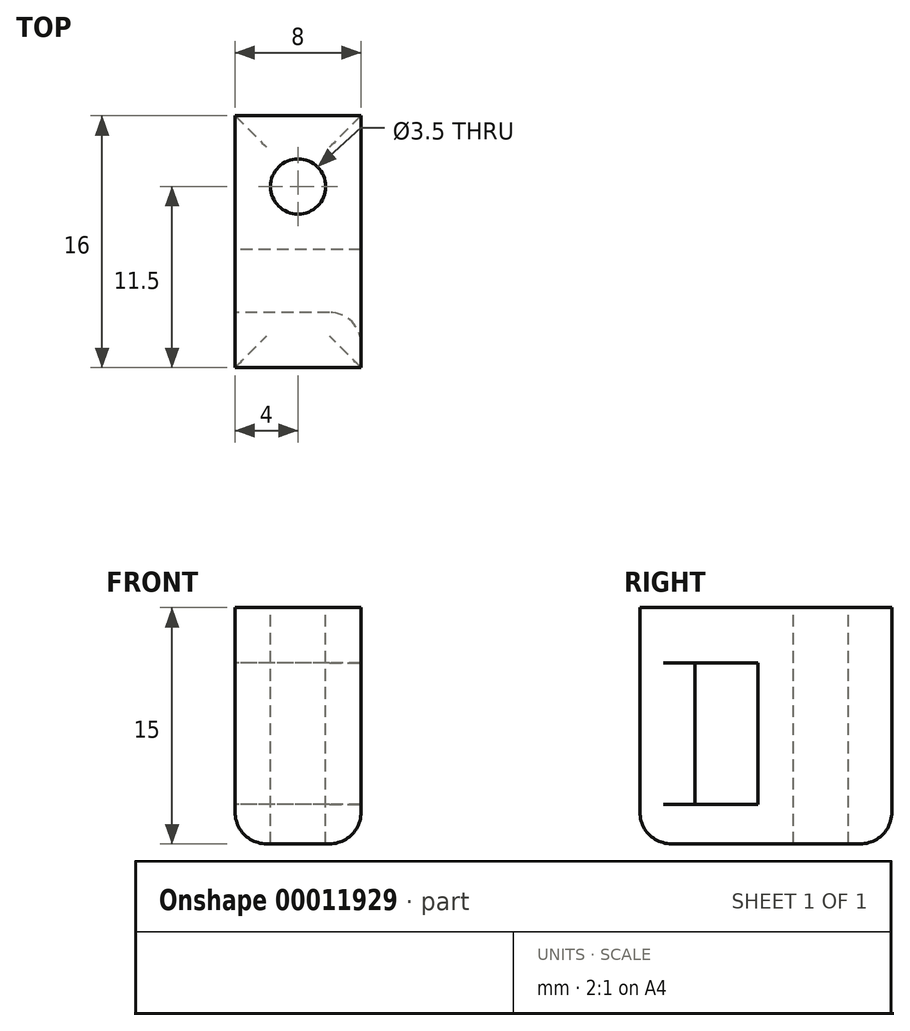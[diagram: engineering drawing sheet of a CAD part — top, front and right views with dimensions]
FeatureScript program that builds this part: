
annotation { "Feature Type Name" : "Feature", "Feature Type Description" : "" }
export const myFeature = defineFeature(function(context is Context, id is Id, definition is map)
    precondition{}
    {
        {
            var Q0;
            Q0=qCreatedBy(makeId("Top.planeOp"),FACE);
            var sketch = newSketch(context, id + "F0", { "sketchPlane" : qUnion([Q0])});
            skLineSegment(sketch, "E0.rect.bottom", {"start": v(-4, 8) * mm, "end": v(4, 8) * mm});
            skLineSegment(sketch, "E0.rect.top", {"start": v(-4, -8) * mm, "end": v(4, -8) * mm});
            skLineSegment(sketch, "E0.rect.left", {"start": v(-4, 8) * mm, "end": v(-4, -8) * mm});
            skLineSegment(sketch, "E0.rect.right", {"start": v(4, 8) * mm, "end": v(4, -8) * mm});
            skPoint(sketch, "E0.rect.middle", {"position": v(0, 0) * mm});
            skSolve(sketch);
        }
        {
            var Q0;
            Q0=makeQuery(id+"F0.imprint","IMPRINT",FACE,{"disambiguationData":[TD([[makeQuery(id+"F0.imprint","IMPRINT",EDGE,{"derivedFrom":sQuery(id+"F0.wireOp",EDGE,"E0.rect.bottom")}),-1.0]])]});
            extrude(context, id + "F1", {"entities" : qUnion([Q0]), "depth" : 15 * mm});
        }
        {
            var Q0;
            Q0=makeQuery(id+"F1.opExtrude","CAP_FACE",FACE,{"disambiguationData":[OSD([sQuery(id+"F0.wireOp",EDGE,"E0.rect.bottom"),sQuery(id+"F0.wireOp",EDGE,"E0.rect.top"),sQuery(id+"F0.wireOp",EDGE,"E0.rect.left"),sQuery(id+"F0.wireOp",EDGE,"E0.rect.right")])],"isStart":false});
            var sketch = newSketch(context, id + "F2", { "sketchPlane" : qUnion([Q0])});
            skCircle(sketch, "E1", {"center": v(0, 3.5) * mm, "radius": 1.75 * mm});
            skSolve(sketch);
        }
        {
            var Q0;
            Q0=makeQuery(id+"F1.opExtrude","SWEPT_FACE",FACE,{"disambiguationData":[OSD([sQuery(id+"F0.wireOp",EDGE,"E0.rect.left")])]});
            var sketch = newSketch(context, id + "F3", { "sketchPlane" : qUnion([Q0])});
            skLineSegment(sketch, "E2.bottom", {"start": v(0.5, 11.5) * mm, "end": v(4.5, 11.5) * mm});
            skLineSegment(sketch, "E2.top", {"start": v(0.5, 2.5) * mm, "end": v(4.5, 2.5) * mm});
            skLineSegment(sketch, "E2.left", {"start": v(0.5, 11.5) * mm, "end": v(0.5, 2.5) * mm});
            skLineSegment(sketch, "E2.right", {"start": v(4.5, 11.5) * mm, "end": v(4.5, 2.5) * mm});
            skSolve(sketch);
        }
        {
            var Q0;
            Q0 = qSketchRegion(id + "F3", true);
            extrude(context, id + "F4", {"entities" : qUnion([Q0]), "operationType" : NewBodyOperationType.REMOVE, "endBound" : BoundingType.THROUGH_ALL, "oppositeDirection" : true, "depth" : 25 * mm});
        }
        {
            var Q0;
            Q0=makeQuery(id+"F4.boolean.opBoolean","COPY",EDGE,{"derivedFrom":makeQuery(id+"F4.opExtrude","CAP_EDGE",EDGE,{"disambiguationData":[OSD([sQuery(id+"F3.wireOp",EDGE,"E2.right")])],"isStart":true})});
            var Q1;
            Q1=makeQuery(id+"F4.boolean.opBoolean","INTERSECT",EDGE,{"derivedFrom":[makeQuery(id+"F1.opExtrude","SWEPT_FACE",FACE,{"disambiguationData":[OSD([sQuery(id+"F0.wireOp",EDGE,"E0.rect.right")])]}),makeQuery(id+"F4.opExtrude","SWEPT_FACE",FACE,{"disambiguationData":[OSD([sQuery(id+"F3.wireOp",EDGE,"E2.right")])]})]});
            var Q2;
            Q2=makeQuery(id+"F1.opExtrude","CAP_EDGE",EDGE,{"disambiguationData":[OSD([sQuery(id+"F0.wireOp",EDGE,"E0.rect.top")])],"isStart":true});
            var Q3;
            Q3=makeQuery(id+"F1.opExtrude","CAP_EDGE",EDGE,{"disambiguationData":[OSD([sQuery(id+"F0.wireOp",EDGE,"E0.rect.bottom")])],"isStart":true});
            var Q4;
            Q4=makeQuery(id+"F1.opExtrude","CAP_EDGE",EDGE,{"disambiguationData":[OSD([sQuery(id+"F0.wireOp",EDGE,"E0.rect.right")])],"isStart":true});
            var Q5;
            Q5=makeQuery(id+"F1.opExtrude","CAP_EDGE",EDGE,{"disambiguationData":[OSD([sQuery(id+"F0.wireOp",EDGE,"E0.rect.left")])],"isStart":true});
            fillet(context, id + "F5", {"entities" : qUnion([Q0, Q1, Q2, Q3, Q4, Q5]), "radius" : 2 * mm, "tangentPropagation" : true, "allowEdgeOverflow" : false});
        }
        {
            var Q0;
            Q0=makeQuery(id+"F2.imprint","IMPRINT",FACE,{"disambiguationData":[TD([[makeQuery(id+"F2.imprint","IMPRINT",EDGE,{"derivedFrom":sQuery(id+"F2.wireOp",EDGE,"E1")}),1.0]])]});
            extrude(context, id + "F6", {"entities" : qUnion([Q0]), "operationType" : NewBodyOperationType.REMOVE, "endBound" : BoundingType.THROUGH_ALL, "oppositeDirection" : true, "depth" : 25 * mm});
        }
    });
